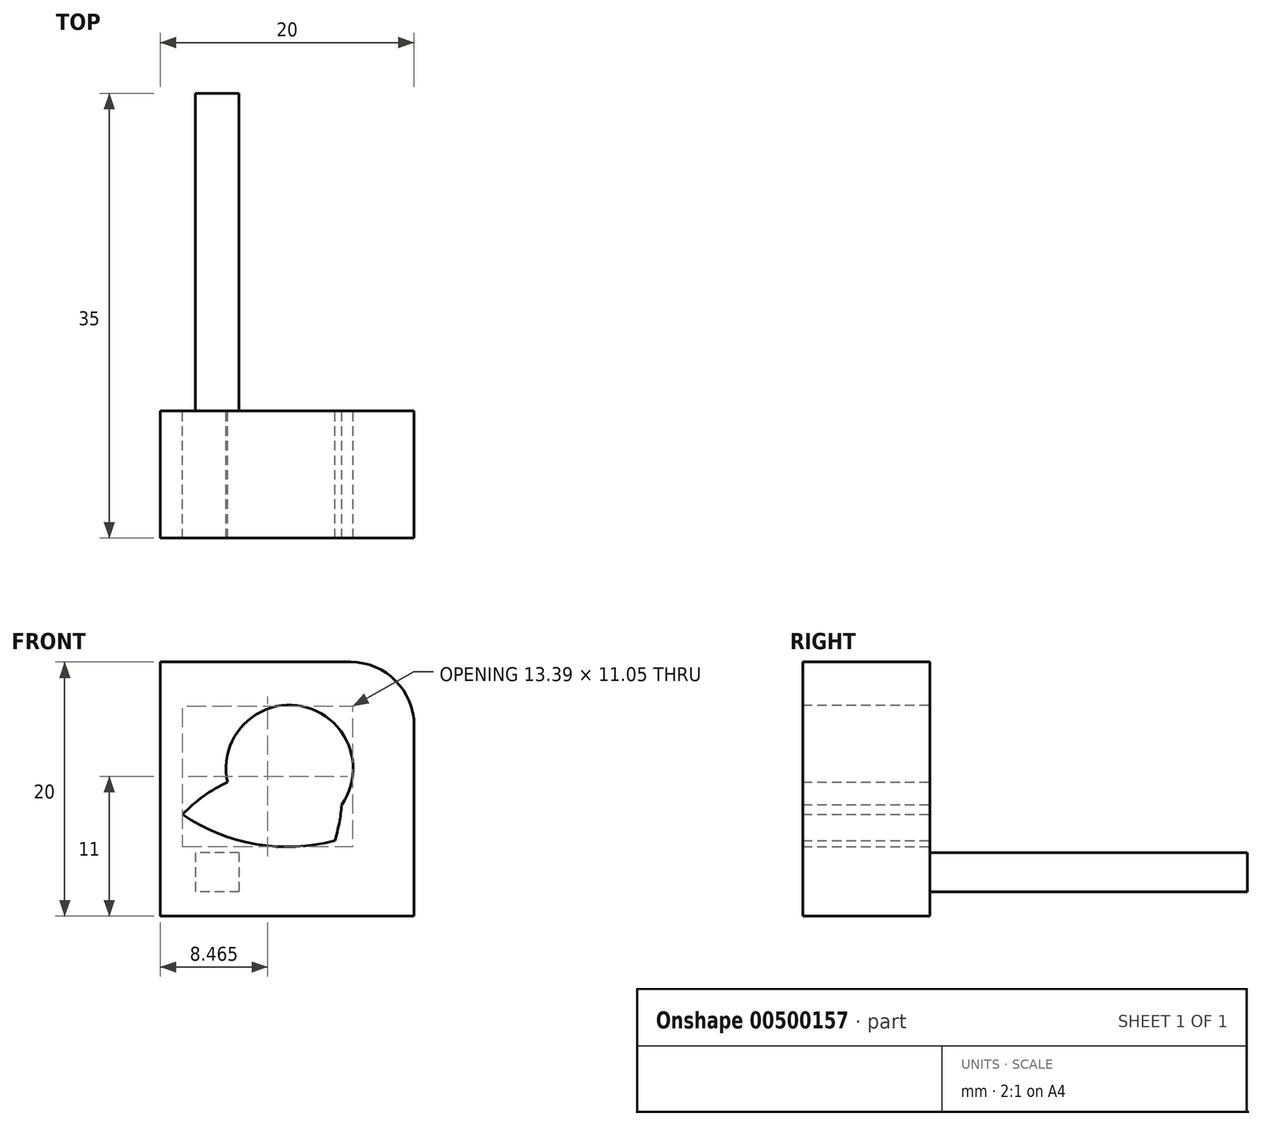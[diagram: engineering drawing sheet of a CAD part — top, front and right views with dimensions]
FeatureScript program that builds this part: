
annotation { "Feature Type Name" : "Feature", "Feature Type Description" : "" }
export const myFeature = defineFeature(function(context is Context, id is Id, definition is map)
    precondition{}
    {
        {
            var Q0;
            Q0=qCreatedBy(makeId("Front.planeOp"),FACE);
            var sketch = newSketch(context, id + "F0", { "sketchPlane" : qUnion([Q0])});
            skLineSegment(sketch, "E0.bottom", {"start": v(-10.2, 8.38) * mm, "end": v(9.8, 8.38) * mm});
            skLineSegment(sketch, "E0.top", {"start": v(-10.2, -11.62) * mm, "end": v(9.8, -11.62) * mm});
            skLineSegment(sketch, "E0.left", {"start": v(-10.2, 8.38) * mm, "end": v(-10.2, -11.62) * mm});
            skLineSegment(sketch, "E0.right", {"start": v(9.8, 8.38) * mm, "end": v(9.8, -11.62) * mm});
            skCircle(sketch, "E1", {"center": v(-0.2, 8.38) * mm, "radius": 14.54 * mm});
            skCircle(sketch, "E2", {"center": v(-10.2, -1.62) * mm, "radius": 14.35 * mm});
            skCircle(sketch, "E3", {"center": v(0, -11.62) * mm, "radius": 11.62 * mm});
            skCircle(sketch, "E4", {"center": v(0, 0) * mm, "radius": 5 * mm});
            skSolve(sketch);
        }
        {
            var Q0;
            {var subQ1=sQuery(id+"F0.wireOp",EDGE,"E0.right");var subQ8=sQuery(id+"F0.wireOp",EDGE,"E0.bottom");var subQ11=makeQuery(id+"F0.imprint","INTERSECT",VERTEX,{"derivedFrom":[subQ8,subQ1]});Q0=makeQuery(id+"F0.imprint","IMPRINT",FACE,{"disambiguationData":[TD([[makeQuery(id+"F0.imprint","IMPRINT",EDGE,{"disambiguationData":[TD([[subQ11,1.0]])],"derivedFrom":subQ8}),-1.0]])]});}
            var Q1;
            {var subQ1=sQuery(id+"F0.wireOp",EDGE,"E0.bottom");var subQ9=sQuery(id+"F0.wireOp",EDGE,"E0.left");var subQ11=makeQuery(id+"F0.imprint","INTERSECT",VERTEX,{"derivedFrom":[subQ1,subQ9]});Q1=makeQuery(id+"F0.imprint","IMPRINT",FACE,{"disambiguationData":[TD([[makeQuery(id+"F0.imprint","IMPRINT",EDGE,{"disambiguationData":[TD([[subQ11,-1.0]])],"derivedFrom":subQ1}),-1.0]])]});}
            var Q2;
            {var subQ1=sQuery(id+"F0.wireOp",EDGE,"E0.top");var subQ5=sQuery(id+"F0.wireOp",EDGE,"E0.left");var subQ6=makeQuery(id+"F0.imprint","INTERSECT",VERTEX,{"derivedFrom":[subQ1,subQ5]});Q2=makeQuery(id+"F0.imprint","IMPRINT",FACE,{"disambiguationData":[TD([[makeQuery(id+"F0.imprint","IMPRINT",EDGE,{"disambiguationData":[TD([[subQ6,-1.0]])],"derivedFrom":subQ1}),1.0]])]});}
            var Q3;
            {var subQ0=sQuery(id+"F0.wireOp",EDGE,"E3");var subQ1=sQuery(id+"F0.wireOp",EDGE,"E1");var subQ2=makeQuery(id+"F0.imprint","INTERSECT",VERTEX,{"disambiguationData":[OD(0.0)],"derivedFrom":[subQ1,subQ0]});Q3=makeQuery(id+"F0.imprint","IMPRINT",FACE,{"disambiguationData":[TD([[makeQuery(id+"F0.imprint","IMPRINT",EDGE,{"disambiguationData":[TD([[subQ2,-1.0]])],"derivedFrom":subQ1}),1.0]])]});}
            var Q4;
            {var subQ0=sQuery(id+"F0.wireOp",EDGE,"E1");var subQ1=sQuery(id+"F0.wireOp",EDGE,"E0.left");var subQ2=makeQuery(id+"F0.imprint","INTERSECT",VERTEX,{"derivedFrom":[subQ1,subQ0]});Q4=makeQuery(id+"F0.imprint","IMPRINT",FACE,{"disambiguationData":[TD([[makeQuery(id+"F0.imprint","IMPRINT",EDGE,{"disambiguationData":[TD([[subQ2,-1.0]])],"derivedFrom":subQ1}),1.0]])]});}
            var Q5;
            {var subQ0=sQuery(id+"F0.wireOp",EDGE,"E2");var subQ1=sQuery(id+"F0.wireOp",EDGE,"E1");var subQ2=makeQuery(id+"F0.imprint","INTERSECT",VERTEX,{"disambiguationData":[OD(1.0)],"derivedFrom":[subQ1,subQ0]});Q5=makeQuery(id+"F0.imprint","IMPRINT",FACE,{"disambiguationData":[TD([[makeQuery(id+"F0.imprint","IMPRINT",EDGE,{"disambiguationData":[TD([[subQ2,-1.0]])],"derivedFrom":subQ1}),1.0]])]});}
            var Q6;
            {var subQ1=sQuery(id+"F0.wireOp",EDGE,"E0.top");var subQ5=sQuery(id+"F0.wireOp",EDGE,"E0.right");var subQ6=makeQuery(id+"F0.imprint","INTERSECT",VERTEX,{"derivedFrom":[subQ1,subQ5]});Q6=makeQuery(id+"F0.imprint","IMPRINT",FACE,{"disambiguationData":[TD([[makeQuery(id+"F0.imprint","IMPRINT",EDGE,{"disambiguationData":[TD([[subQ6,1.0]])],"derivedFrom":subQ1}),1.0]])]});}
            var Q7;
            {var subQ0=sQuery(id+"F0.wireOp",EDGE,"E1");var subQ1=sQuery(id+"F0.wireOp",EDGE,"E0.right");var subQ2=makeQuery(id+"F0.imprint","INTERSECT",VERTEX,{"derivedFrom":[subQ1,subQ0]});Q7=makeQuery(id+"F0.imprint","IMPRINT",FACE,{"disambiguationData":[TD([[makeQuery(id+"F0.imprint","IMPRINT",EDGE,{"disambiguationData":[TD([[subQ2,-1.0]])],"derivedFrom":subQ1}),-1.0]])]});}
            extrude(context, id + "F1", {"entities" : qUnion([Q0, Q1, Q2, Q3, Q4, Q5, Q6, Q7]), "depth" : 10 * mm});
        }
        {
            var Q0;
            Q0=makeQuery(id+"F1.opExtrude","SWEPT_EDGE",EDGE,{"disambiguationData":[OSD([sQuery(id+"F0.wireOp",EDGE,"E0.bottom"),sQuery(id+"F0.wireOp",EDGE,"E0.right")])]});
            fillet(context, id + "F2", {"entities" : qUnion([Q0]), "radius" : 5 * mm, "tangentPropagation" : true, "allowEdgeOverflow" : false});
        }
        {
            var Q0;
            Q0=makeQuery(id+"F1.opExtrude","CAP_FACE",FACE,{"disambiguationData":[OSD([sQuery(id+"F0.wireOp",EDGE,"E0.bottom"),sQuery(id+"F0.wireOp",EDGE,"E0.top"),sQuery(id+"F0.wireOp",EDGE,"E0.left"),sQuery(id+"F0.wireOp",EDGE,"E0.right"),sQuery(id+"F0.wireOp",EDGE,"E4")])],"isStart":true});
            var sketch = newSketch(context, id + "F3", { "sketchPlane" : qUnion([Q0])});
            skLineSegment(sketch, "E5.bottom", {"start": v(3.98, -6.61) * mm, "end": v(7.43, -6.61) * mm});
            skLineSegment(sketch, "E5.top", {"start": v(3.98, -9.7) * mm, "end": v(7.43, -9.7) * mm});
            skLineSegment(sketch, "E5.left", {"start": v(3.98, -6.61) * mm, "end": v(3.98, -9.7) * mm});
            skLineSegment(sketch, "E5.right", {"start": v(7.43, -6.61) * mm, "end": v(7.43, -9.7) * mm});
            skSolve(sketch);
        }
        {
            var Q0;
            Q0=makeQuery(id+"F3.imprint","IMPRINT",FACE,{"disambiguationData":[TD([[makeQuery(id+"F3.imprint","IMPRINT",EDGE,{"derivedFrom":sQuery(id+"F3.wireOp",EDGE,"E5.bottom")}),-1.0]])]});
            extrude(context, id + "F4", {"entities" : qUnion([Q0]), "operationType" : NewBodyOperationType.ADD, "depth" : 25 * mm, "offsetDistance" : 25 * mm});
        }
    });
